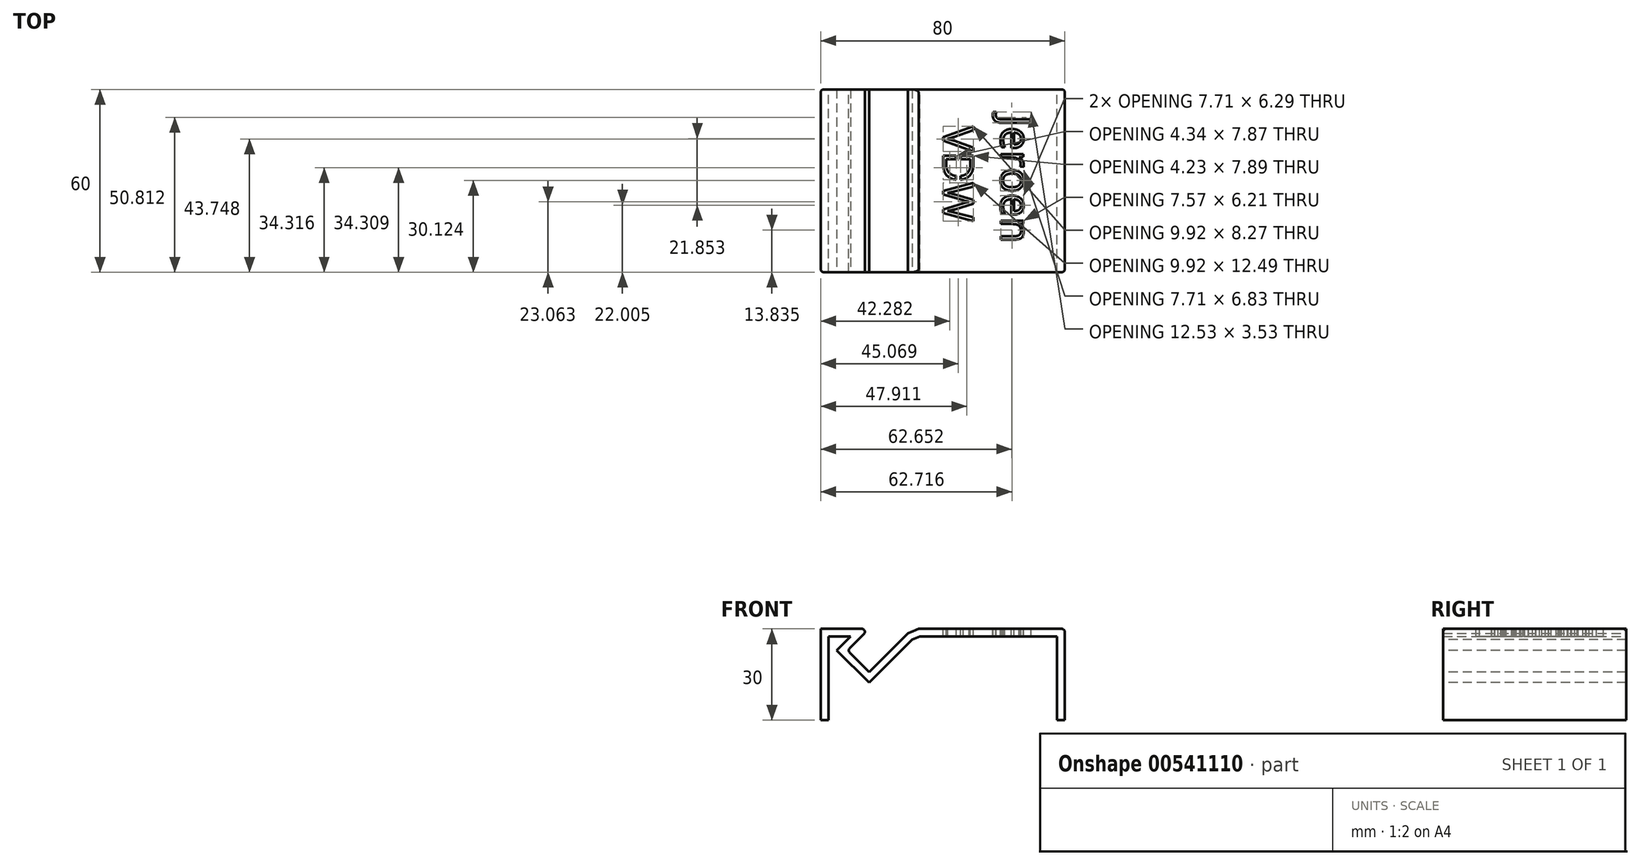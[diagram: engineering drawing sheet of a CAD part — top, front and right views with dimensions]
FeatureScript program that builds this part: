
annotation { "Feature Type Name" : "Feature", "Feature Type Description" : "" }
export const myFeature = defineFeature(function(context is Context, id is Id, definition is map)
    precondition{}
    {
        {
            var Q0;
            Q0=qCreatedBy(makeId("Top.planeOp"),FACE);
            var sketch = newSketch(context, id + "F0", { "sketchPlane" : qUnion([Q0])});
            skLineSegment(sketch, "E0.bottom", {"start": v(-40, -30) * mm, "end": v(40, -30) * mm});
            skLineSegment(sketch, "E0.top", {"start": v(-40, 30) * mm, "end": v(40, 30) * mm});
            skLineSegment(sketch, "E0.left", {"start": v(-40, -30) * mm, "end": v(-40, 30) * mm});
            skLineSegment(sketch, "E0.right", {"start": v(40, -30) * mm, "end": v(40, 30) * mm});
            skPoint(sketch, "E0.middle", {"position": v(0, 0) * mm});
            skSolve(sketch);
        }
        {
            var Q0;
            Q0 = qSketchRegion(id + "F0", true);
            extrude(context, id + "F1", {"entities" : qUnion([Q0]), "depth" : 30 * mm, "offsetDistance" : 25 * mm});
        }
        {
            var Q0;
            Q0=makeQuery(id+"F1.opExtrude","SWEPT_FACE",FACE,{"disambiguationData":[OSD([sQuery(id+"F0.wireOp",EDGE,"E0.bottom")])]});
            var sketch = newSketch(context, id + "F2", { "sketchPlane" : qUnion([Q0])});
            skLineSegment(sketch, "E1.bottom", {"start": v(-17.07, 37.07) * mm, "end": v(-31.21, 22.93) * mm});
            skLineSegment(sketch, "E1.top", {"start": v(-10, 30) * mm, "end": v(-24.14, 15.86) * mm});
            skLineSegment(sketch, "E1.left", {"start": v(-17.07, 37.07) * mm, "end": v(-10, 30) * mm});
            skLineSegment(sketch, "E1.right", {"start": v(-31.21, 22.93) * mm, "end": v(-24.14, 15.86) * mm});
            skSolve(sketch);
        }
        {
            var Q0;
            Q0 = qSketchRegion(id + "F2", true);
            extrude(context, id + "F3", {"entities" : qUnion([Q0]), "operationType" : NewBodyOperationType.REMOVE, "oppositeDirection" : true, "depth" : 77.5 * mm, "offsetDistance" : 25 * mm});
        }
        {
            var Q0;
            Q0=makeQuery(id+"F3.boolean.opBoolean","COPY",EDGE,{"derivedFrom":makeQuery(id+"F3.opExtrude","SWEPT_EDGE",EDGE,{"disambiguationData":[OSD([sQuery(id+"F0.wireOp",EDGE,"E0.bottom"),sQuery(id+"F2.wireOp",EDGE,"E1.top"),sQuery(id+"F2.wireOp",EDGE,"E1.left")])]})});
            chamfer(context, id + "F4", {"entities" : qUnion([Q0]), "width" : 5 * mm, "tangentPropagation" : true});
        }
        {
            var Q0;
            Q0=makeQuery(id+"F1.opExtrude","CAP_FACE",FACE,{"disambiguationData":[OSD([sQuery(id+"F0.wireOp",EDGE,"E0.bottom"),sQuery(id+"F0.wireOp",EDGE,"E0.top"),sQuery(id+"F0.wireOp",EDGE,"E0.left"),sQuery(id+"F0.wireOp",EDGE,"E0.right")])],"isStart":true});
            shell(context, id + "F5", {"entities" : qUnion([Q0]), "thickness" : 2.5 * mm});
        }
        {
            var Q0;
            {var subQ0=sQuery(id+"F0.wireOp",EDGE,"E0.bottom");Q0=makeQuery(id+"F5.opShell","OFFSET_FACE",FACE,{"disambiguationData":[OSD([subQ0]),TDD([makeQuery(id+"F1.opExtrude","SWEPT_FACE",FACE,{"disambiguationData":[OSD([subQ0])]})])]});}
            extrude(context, id + "F6", {"entities" : qUnion([Q0]), "operationType" : NewBodyOperationType.REMOVE, "oppositeDirection" : true, "depth" : 25 * mm, "offsetDistance" : 25 * mm});
        }
        {
            var Q0;
            {var subQ0=sQuery(id+"F0.wireOp",EDGE,"E0.bottom");var subQ1=sQuery(id+"F0.wireOp",EDGE,"E0.right");Q0=makeQuery(id+"F3.boolean.opBoolean","SPLIT",EDGE,{"disambiguationData":[TD([makeQuery(id+"F1.opExtrude","SWEPT_FACE",FACE,{"disambiguationData":[OSD([subQ1])]})])],"derivedFrom":makeQuery(id+"F1.opExtrude","CAP_EDGE",EDGE,{"disambiguationData":[OSD([subQ0])],"isStart":false})});}
            var Q1;
            Q1=makeQuery(id+"F1.opExtrude","CAP_EDGE",EDGE,{"disambiguationData":[OSD([sQuery(id+"F0.wireOp",EDGE,"E0.right")])],"isStart":false});
            var Q2;
            {var subQ0=sQuery(id+"F0.wireOp",EDGE,"E0.right");var subQ1=sQuery(id+"F0.wireOp",EDGE,"E0.top");Q2=makeQuery(id+"F3.boolean.opBoolean","SPLIT",EDGE,{"disambiguationData":[TD([makeQuery(id+"F1.opExtrude","SWEPT_FACE",FACE,{"disambiguationData":[OSD([subQ0])]})])],"derivedFrom":makeQuery(id+"F1.opExtrude","CAP_EDGE",EDGE,{"disambiguationData":[OSD([subQ1])],"isStart":false})});}
            var Q3;
            Q3=makeQuery(id+"F1.opExtrude","SWEPT_EDGE",EDGE,{"disambiguationData":[OSD([sQuery(id+"F0.wireOp",EDGE,"E0.top"),sQuery(id+"F0.wireOp",EDGE,"E0.right")])]});
            var Q4;
            Q4=makeQuery(id+"F1.opExtrude","SWEPT_EDGE",EDGE,{"disambiguationData":[OSD([sQuery(id+"F0.wireOp",EDGE,"E0.top"),sQuery(id+"F0.wireOp",EDGE,"E0.left")])]});
            var Q5;
            Q5=makeQuery(id+"F1.opExtrude","SWEPT_EDGE",EDGE,{"disambiguationData":[OSD([sQuery(id+"F0.wireOp",EDGE,"E0.bottom"),sQuery(id+"F0.wireOp",EDGE,"E0.right")])]});
            var Q6;
            Q6=makeQuery(id+"F1.opExtrude","SWEPT_EDGE",EDGE,{"disambiguationData":[OSD([sQuery(id+"F0.wireOp",EDGE,"E0.bottom"),sQuery(id+"F0.wireOp",EDGE,"E0.left")])]});
            var Q7;
            Q7=makeQuery(id+"F3.boolean.opBoolean","COPY",EDGE,{"derivedFrom":makeQuery(id+"F3.opExtrude","SWEPT_EDGE",EDGE,{"disambiguationData":[OSD([sQuery(id+"F2.wireOp",EDGE,"E1.bottom"),sQuery(id+"F2.wireOp",EDGE,"E1.right")])]})});
            var Q8;
            Q8=makeQuery(id+"F3.boolean.opBoolean","INTERSECT",EDGE,{"derivedFrom":[makeQuery(id+"F1.opExtrude","CAP_FACE",FACE,{"disambiguationData":[OSD([sQuery(id+"F0.wireOp",EDGE,"E0.bottom"),sQuery(id+"F0.wireOp",EDGE,"E0.top"),sQuery(id+"F0.wireOp",EDGE,"E0.left"),sQuery(id+"F0.wireOp",EDGE,"E0.right")])],"isStart":false}),makeQuery(id+"F3.opExtrude","SWEPT_FACE",FACE,{"disambiguationData":[OSD([sQuery(id+"F2.wireOp",EDGE,"E1.bottom")])]})]});
            fillet(context, id + "F7", {"entities" : qUnion([Q0, Q1, Q2, Q3, Q4, Q5, Q6, Q7, Q8]), "radius" : 1 * mm, "tangentPropagation" : true, "allowEdgeOverflow" : false});
        }
        {
            var Q0;
            {var subQ0=sQuery(id+"F0.wireOp",EDGE,"E0.top");Q0=makeQuery(id+"F5.opShell","OFFSET_FACE",FACE,{"disambiguationData":[OSD([subQ0]),TDD([makeQuery(id+"F1.opExtrude","SWEPT_FACE",FACE,{"disambiguationData":[OSD([subQ0])]})])]});}
            extrude(context, id + "F8", {"entities" : qUnion([Q0]), "operationType" : NewBodyOperationType.REMOVE, "oppositeDirection" : true, "depth" : 25 * mm, "offsetDistance" : 25 * mm});
        }
        {
            var Q0;
            {var subQ0=sQuery(id+"F0.wireOp",EDGE,"E0.bottom");var subQ1=sQuery(id+"F0.wireOp",EDGE,"E0.right");var subQ2=sQuery(id+"F0.wireOp",EDGE,"E0.top");Q0=makeQuery(id+"F3.boolean.opBoolean","SPLIT",FACE,{"disambiguationData":[TD([makeQuery(id+"F1.opExtrude","SWEPT_FACE",FACE,{"disambiguationData":[OSD([subQ1])]})])],"derivedFrom":makeQuery(id+"F1.opExtrude","CAP_FACE",FACE,{"disambiguationData":[OSD([subQ0,subQ2,sQuery(id+"F0.wireOp",EDGE,"E0.left"),subQ1])],"isStart":false})});}
            var sketch = newSketch(context, id + "F9", { "sketchPlane" : qUnion([Q0])});
            skText(sketch, "E2", { "text": "Jeroen\n VDW", "fontName": "OpenSans-Regular.ttf"});
            skLineSegment(sketch, "E3", {"start": v(39, 0) * mm, "end": v(29, 0.11) * mm, "construction": true});
            const initialGuessF9  = {"E2": [0.019, 0.02149, 0, -1, 0.01]};
            skSetInitialGuess(sketch, initialGuessF9);
            skSolve(sketch);
        }
        {
            var Q0;
            Q0 = qSketchRegion(id + "F9", true);
            extrude(context, id + "F10", {"entities" : qUnion([Q0]), "operationType" : NewBodyOperationType.REMOVE, "endBound" : BoundingType.UP_TO_NEXT, "oppositeDirection" : true, "depth" : 25 * mm, "offsetDistance" : 25 * mm});
        }
        {
            var Q0;
            {var subQ0=sQuery(id+"F0.wireOp",EDGE,"E0.right");var subQ1=sQuery(id+"F0.wireOp",EDGE,"E0.top");var subQ2=sQuery(id+"F0.wireOp",EDGE,"E0.bottom");Q0=makeQuery(id+"F10.boolean.opBoolean","SPLIT",FACE,{"disambiguationData":[TD([makeQuery(id+"F7.opFillet","BLEND_FACE",FACE,{"disambiguationData":[OSD([subQ0])]})])],"derivedFrom":makeQuery(id+"F3.boolean.opBoolean","SPLIT",FACE,{"disambiguationData":[TD([makeQuery(id+"F1.opExtrude","SWEPT_FACE",FACE,{"disambiguationData":[OSD([subQ0])]})])],"derivedFrom":makeQuery(id+"F1.opExtrude","CAP_FACE",FACE,{"disambiguationData":[OSD([subQ2,subQ1,sQuery(id+"F0.wireOp",EDGE,"E0.left"),subQ0])],"isStart":false})})});}
            var sketch = newSketch(context, id + "F11", { "sketchPlane" : qUnion([Q0])});
            skLineSegment(sketch, "E4.bottom", {"start": v(5.82, 8.25) * mm, "end": v(4.32, 8.25) * mm});
            skLineSegment(sketch, "E4.top", {"start": v(5.82, 7.1) * mm, "end": v(4.32, 7.1) * mm});
            skLineSegment(sketch, "E4.left", {"start": v(5.82, 8.25) * mm, "end": v(5.82, 7.1) * mm});
            skLineSegment(sketch, "E4.right", {"start": v(4.32, 8.25) * mm, "end": v(4.32, 7.1) * mm});
            skSolve(sketch);
        }
        {
            var Q0;
            Q0 = qSketchRegion(id + "F11", true);
            var Q1;
            {var subQ0=sQuery(id+"F0.wireOp",EDGE,"E0.top");var subQ2=sQuery(id+"F0.wireOp",EDGE,"E0.bottom");var subQ3=makeQuery(id+"F1.opExtrude","SWEPT_FACE",FACE,{"disambiguationData":[OSD([subQ2])]});var subQ4=sQuery(id+"F0.wireOp",EDGE,"E0.right");var subQ7=sQuery(id+"F0.wireOp",EDGE,"E0.left");var subQ8=makeQuery(id+"F1.opExtrude","CAP_FACE",FACE,{"disambiguationData":[OSD([subQ2,subQ0,subQ7,subQ4])],"isStart":false});var subQ9=makeQuery(id+"F1.opExtrude","SWEPT_FACE",FACE,{"disambiguationData":[OSD([subQ4])]});Q1=makeQuery(id+"F10.boolean.opBoolean","SPLIT",FACE,{"disambiguationData":[TD([subQ3])],"derivedFrom":makeQuery(id+"F8.boolean.opBoolean","MERGE",FACE,{"derivedFrom":[makeQuery(id+"F6.boolean.opBoolean","MERGE",FACE,{"derivedFrom":[makeQuery(id+"F5.opShell","OFFSET_FACE",FACE,{"disambiguationData":[OSD([subQ2,subQ0,subQ7,subQ4]),TDD([makeQuery(id+"F3.boolean.opBoolean","SPLIT",FACE,{"disambiguationData":[TD([subQ9])],"derivedFrom":subQ8})])]}),makeQuery(id+"F6.opExtrude","SWEPT_FACE",FACE,{"disambiguationData":[OSD([subQ2]),TDD([makeQuery(id+"F5.opShell","OFFSET_EDGE",EDGE,{"disambiguationData":[OSD([subQ2]),TDD([makeQuery(id+"F3.boolean.opBoolean","SPLIT",EDGE,{"disambiguationData":[TD([subQ9])],"derivedFrom":makeQuery(id+"F1.opExtrude","CAP_EDGE",EDGE,{"disambiguationData":[OSD([subQ2])],"isStart":false})})])]})])]})]}),makeQuery(id+"F8.opExtrude","SWEPT_FACE",FACE,{"disambiguationData":[OSD([subQ0]),TDD([makeQuery(id+"F5.opShell","OFFSET_EDGE",EDGE,{"disambiguationData":[OSD([subQ0]),TDD([makeQuery(id+"F3.boolean.opBoolean","SPLIT",EDGE,{"disambiguationData":[TD([subQ9])],"derivedFrom":makeQuery(id+"F1.opExtrude","CAP_EDGE",EDGE,{"disambiguationData":[OSD([subQ0])],"isStart":false})})])]})])]})]})});}
            extrude(context, id + "F12", {"entities" : qUnion([Q0]), "operationType" : NewBodyOperationType.ADD, "endBound" : BoundingType.UP_TO_SURFACE, "oppositeDirection" : true, "depth" : 25 * mm, "endBoundEntityFace" : qUnion([Q1]), "offsetDistance" : 25 * mm});
        }
        {
            var Q0;
            {var subQ0=sQuery(id+"F0.wireOp",EDGE,"E0.bottom");var subQ1=sQuery(id+"F0.wireOp",EDGE,"E0.right");var subQ2=sQuery(id+"F0.wireOp",EDGE,"E0.top");var subQ4=makeQuery(id+"F3.boolean.opBoolean","SPLIT",FACE,{"disambiguationData":[TD([makeQuery(id+"F1.opExtrude","SWEPT_FACE",FACE,{"disambiguationData":[OSD([subQ1])]})])],"derivedFrom":makeQuery(id+"F1.opExtrude","CAP_FACE",FACE,{"disambiguationData":[OSD([subQ0,subQ2,sQuery(id+"F0.wireOp",EDGE,"E0.left"),subQ1])],"isStart":false})});Q0=makeQuery(id+"F12.boolean.opBoolean","MERGE",FACE,{"derivedFrom":[makeQuery(id+"F10.boolean.opBoolean","SPLIT",FACE,{"disambiguationData":[TD([makeQuery(id+"F7.opFillet","BLEND_FACE",FACE,{"disambiguationData":[OSD([subQ1])]})])],"derivedFrom":subQ4}),makeQuery(id+"F10.boolean.opBoolean","SPLIT",FACE,{"disambiguationData":[TD([makeQuery(id+"F10.opExtrude","SWEPT_FACE",FACE,{"disambiguationData":[OSD([sQuery(id+"F9.wireOp",EDGE,"E2.sketch_text.stroke-111")])]})])],"derivedFrom":subQ4}),makeQuery(id+"F12.opExtrude","CAP_FACE",FACE,{"disambiguationData":[OSD([sQuery(id+"F11.wireOp",EDGE,"E4.bottom"),sQuery(id+"F11.wireOp",EDGE,"E4.top"),sQuery(id+"F11.wireOp",EDGE,"E4.left"),sQuery(id+"F11.wireOp",EDGE,"E4.right")])],"isStart":true})]});}
            var sketch = newSketch(context, id + "F13", { "sketchPlane" : qUnion([Q0])});
            skLineSegment(sketch, "E5.bottom", {"start": v(5.82, 1.59) * mm, "end": v(4.32, 1.59) * mm});
            skLineSegment(sketch, "E5.top", {"start": v(5.82, 0.34) * mm, "end": v(4.32, 0.34) * mm});
            skLineSegment(sketch, "E5.left", {"start": v(5.82, 1.59) * mm, "end": v(5.82, 0.34) * mm});
            skLineSegment(sketch, "E5.right", {"start": v(4.32, 1.59) * mm, "end": v(4.32, 0.34) * mm});
            skSolve(sketch);
        }
        {
            var Q0;
            {var subQ3=sQuery(id+"F13.wireOp",EDGE,"E5.right");var subQ6=sQuery(id+"F13.wireOp",EDGE,"E5.bottom");var subQ12=makeQuery(id+"F13.imprint","INTERSECT",VERTEX,{"derivedFrom":[subQ6,subQ3]});Q0=makeQuery(id+"F13.imprint","IMPRINT",FACE,{"disambiguationData":[TD([[makeQuery(id+"F13.imprint","IMPRINT",EDGE,{"disambiguationData":[TD([[subQ12,1.0]])],"derivedFrom":subQ6}),1.0]])]});}
            var Q1;
            {var subQ0=sQuery(id+"F0.wireOp",EDGE,"E0.right");var subQ1=sQuery(id+"F0.wireOp",EDGE,"E0.left");var subQ2=sQuery(id+"F0.wireOp",EDGE,"E0.top");var subQ3=sQuery(id+"F0.wireOp",EDGE,"E0.bottom");var subQ4=makeQuery(id+"F1.opExtrude","CAP_FACE",FACE,{"disambiguationData":[OSD([subQ3,subQ2,subQ1,subQ0])],"isStart":false});var subQ6=makeQuery(id+"F1.opExtrude","SWEPT_FACE",FACE,{"disambiguationData":[OSD([subQ0])]});var subQ9=makeQuery(id+"F1.opExtrude","SWEPT_FACE",FACE,{"disambiguationData":[OSD([subQ3])]});var subQ10=makeQuery(id+"F8.boolean.opBoolean","MERGE",FACE,{"derivedFrom":[makeQuery(id+"F6.boolean.opBoolean","MERGE",FACE,{"derivedFrom":[makeQuery(id+"F5.opShell","OFFSET_FACE",FACE,{"disambiguationData":[OSD([subQ3,subQ2,subQ1,subQ0]),TDD([makeQuery(id+"F3.boolean.opBoolean","SPLIT",FACE,{"disambiguationData":[TD([subQ6])],"derivedFrom":subQ4})])]}),makeQuery(id+"F6.opExtrude","SWEPT_FACE",FACE,{"disambiguationData":[OSD([subQ3]),TDD([makeQuery(id+"F5.opShell","OFFSET_EDGE",EDGE,{"disambiguationData":[OSD([subQ3]),TDD([makeQuery(id+"F3.boolean.opBoolean","SPLIT",EDGE,{"disambiguationData":[TD([subQ6])],"derivedFrom":makeQuery(id+"F1.opExtrude","CAP_EDGE",EDGE,{"disambiguationData":[OSD([subQ3])],"isStart":false})})])]})])]})]}),makeQuery(id+"F8.opExtrude","SWEPT_FACE",FACE,{"disambiguationData":[OSD([subQ2]),TDD([makeQuery(id+"F5.opShell","OFFSET_EDGE",EDGE,{"disambiguationData":[OSD([subQ2]),TDD([makeQuery(id+"F3.boolean.opBoolean","SPLIT",EDGE,{"disambiguationData":[TD([subQ6])],"derivedFrom":makeQuery(id+"F1.opExtrude","CAP_EDGE",EDGE,{"disambiguationData":[OSD([subQ2])],"isStart":false})})])]})])]})]});Q1=makeQuery(id+"F12.boolean.opBoolean","MERGE",FACE,{"derivedFrom":[makeQuery(id+"F10.boolean.opBoolean","SPLIT",FACE,{"disambiguationData":[TD([subQ9])],"derivedFrom":subQ10}),makeQuery(id+"F10.boolean.opBoolean","SPLIT",FACE,{"disambiguationData":[TD([makeQuery(id+"F10.opExtrude","SWEPT_FACE",FACE,{"disambiguationData":[OSD([sQuery(id+"F9.wireOp",EDGE,"E2.sketch_text.stroke-111")])]})])],"derivedFrom":subQ10}),makeQuery(id+"F12.opExtrude","CAP_FACE",FACE,{"disambiguationData":[OSD([sQuery(id+"F11.wireOp",EDGE,"E4.bottom"),sQuery(id+"F11.wireOp",EDGE,"E4.top"),sQuery(id+"F11.wireOp",EDGE,"E4.left"),sQuery(id+"F11.wireOp",EDGE,"E4.right")])],"isStart":false})]});}
            extrude(context, id + "F14", {"entities" : qUnion([Q0]), "operationType" : NewBodyOperationType.ADD, "endBound" : BoundingType.UP_TO_SURFACE, "oppositeDirection" : true, "depth" : 25 * mm, "endBoundEntityFace" : qUnion([Q1]), "offsetDistance" : 25 * mm});
        }
    });
